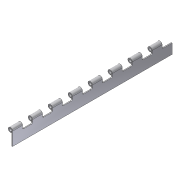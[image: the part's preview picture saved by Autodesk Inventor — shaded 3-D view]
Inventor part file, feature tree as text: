
AUTODESK INVENTOR PART (.ipt)
format: ipt  version: 2012 (Build 160160000, 160)  size: 142,336 bytes
history: native  units: in
note: dims shown in document units (in); Inventor stores cm internally (conversion verified against a paired STEP export)
features: extrude x2, sketch x2, fillet x1, pattern_linear x1, projected_geometry x1
ambient origin geometry x8: Origin, YZ Plane, XZ Plane, XY Plane, X Axis, Y Axis, Z Axis, Center Point
bodies: Solid1 (feature_tree)
feature tree (7):
  extrude  "Extrusion1"  Depth=0.09in
  extrude  "Extrusion2"  Depth=16.0in TaperAngle=0.0deg
  fillet  "Fillet1"  Radius=1.0in
  pattern_linear  "Rectangular Pattern1"  Spacing1=1.0in  [1 undecoded]
  sketch  "Sketch1"  dims[d0=0.445in d1=0.09in]
  sketch  "Sketch2"  dims[d2=0.09in d3=16.0in d4=0.0in d5=1.0in d6=1.0in d7=0.125in d8=16.0in d9=0.0in d10=0.125in d11=3.1496in d13=2.0in]
  projected_geometry  "Projected Loop1"
note: 1 required parameter value undecoded (feature->parameter linkage not recoverable at this tier; creation-order binding heuristic only, values carry confidence <= 0.55)
